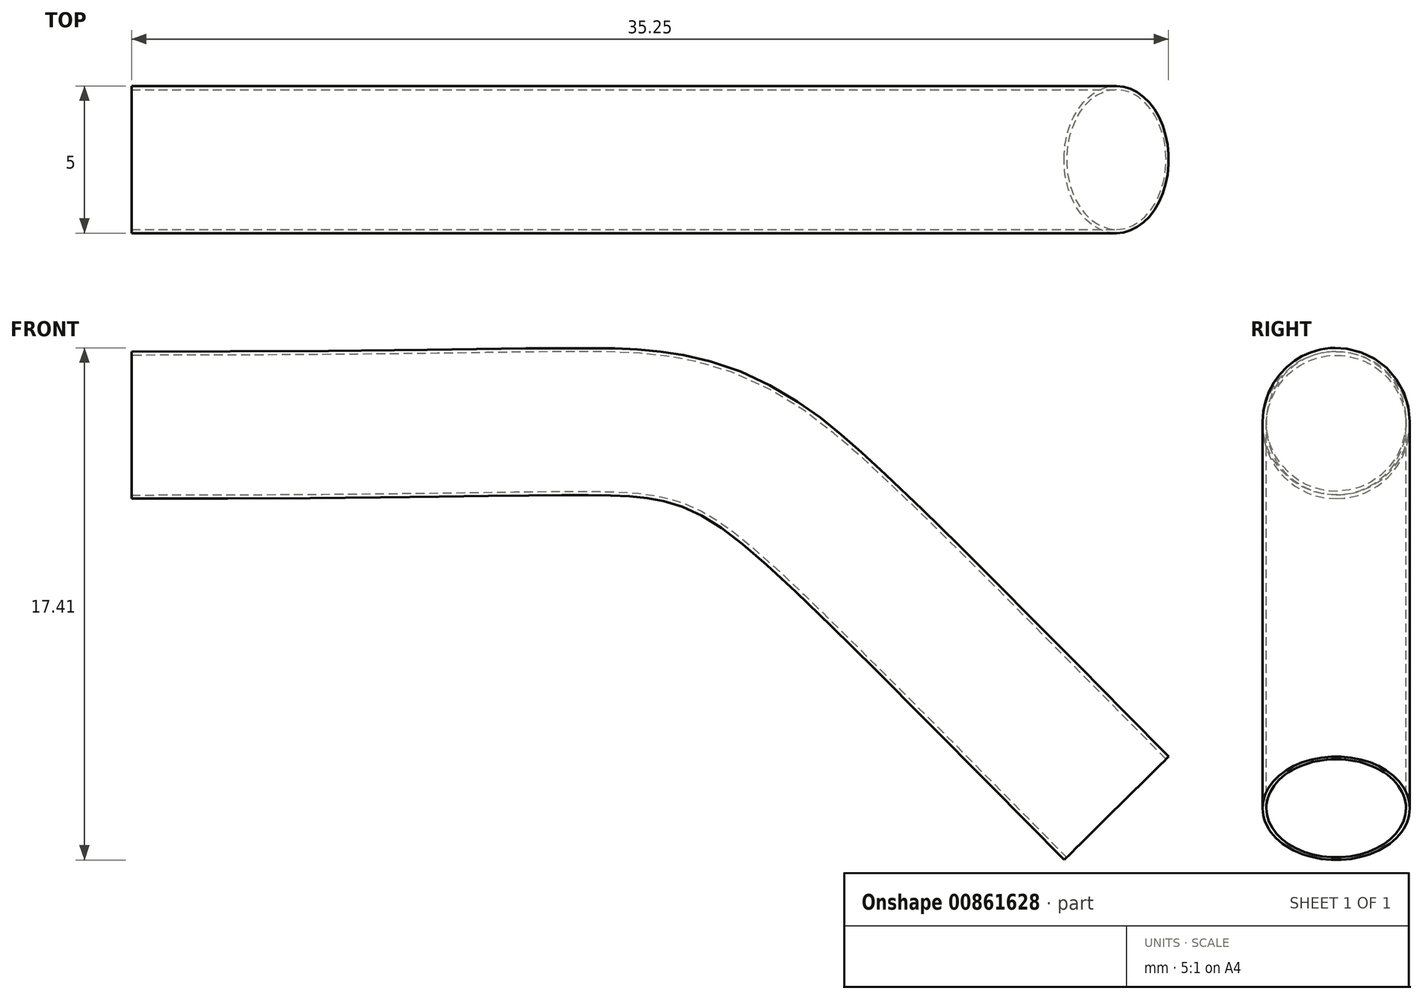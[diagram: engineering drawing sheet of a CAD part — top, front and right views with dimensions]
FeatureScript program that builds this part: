
annotation { "Feature Type Name" : "Feature", "Feature Type Description" : "" }
export const myFeature = defineFeature(function(context is Context, id is Id, definition is map)
    precondition{}
    {
        {
            var Q0;
            Q0=qCreatedBy(makeId("Front.planeOp"),FACE);
            var sketch = newSketch(context, id + "F0", { "sketchPlane" : qUnion([Q0])});
            skFitSpline(sketch, "E0", {"points": [v(-24.8, 0) * mm, v(-7.3, 0) * mm, v(5.66, -11.76) * mm], "startDerivative": vector(80.98, 0) * mm, "endDerivative": vector(62.99, -63.74) * mm});
            skSolve(sketch);
        }
        {
            var Q0;
            Q0=sQuery(id+"F0.wireOp",EDGE,"E0");
            var Q1;
            Q1=sQuery(id+"F0.wireOp",VERTEX,"E0.end");
            cPlane(context, id + "F1", {"entities" : qUnion([Q0, Q1]), "cplaneType" : CPlaneType.CURVE_POINT, "offset" : 25 * mm, "width" : 150 * mm, "height" : 150 * mm});
        }
        {
            var Q0;
            Q0=qCreatedBy(id+"F1.planeOp",FACE);
            var sketch = newSketch(context, id + "F2", { "sketchPlane" : qUnion([Q0])});
            skCircle(sketch, "E1", {"center": v(0, 0.03) * mm, "radius": 2.5 * mm});
            skSolve(sketch);
        }
        {
            var Q0;
            Q0=makeQuery(id+"F2.imprint","IMPRINT",FACE,{"disambiguationData":[TD([[makeQuery(id+"F2.imprint","IMPRINT",EDGE,{"derivedFrom":sQuery(id+"F2.wireOp",EDGE,"E1")}),1.0]])]});
            var Q1;
            Q1=sQuery(id+"F0.wireOp",EDGE,"E0");
            sweep(context, id + "F3", {"profiles" : qUnion([Q0]), "path" : qUnion([Q1])});
        }
        {
            var Q0;
            Q0=makeQuery(id+"F3.opSweep","CAP_FACE",FACE,{"disambiguationData":[OSD([sQuery(id+"F0.wireOp",VERTEX,"E0.start"),sQuery(id+"F2.wireOp",EDGE,"E1")])],"isStart":false});
            var Q1;
            Q1=makeQuery(id+"F3.opSweep","CAP_FACE",FACE,{"disambiguationData":[OSD([sQuery(id+"F0.wireOp",VERTEX,"E0.end"),sQuery(id+"F2.wireOp",EDGE,"E1")])],"isStart":true});
            shell(context, id + "F4", {"entities" : qUnion([Q0, Q1]), "thickness" : .125 * mm});
        }
    });
